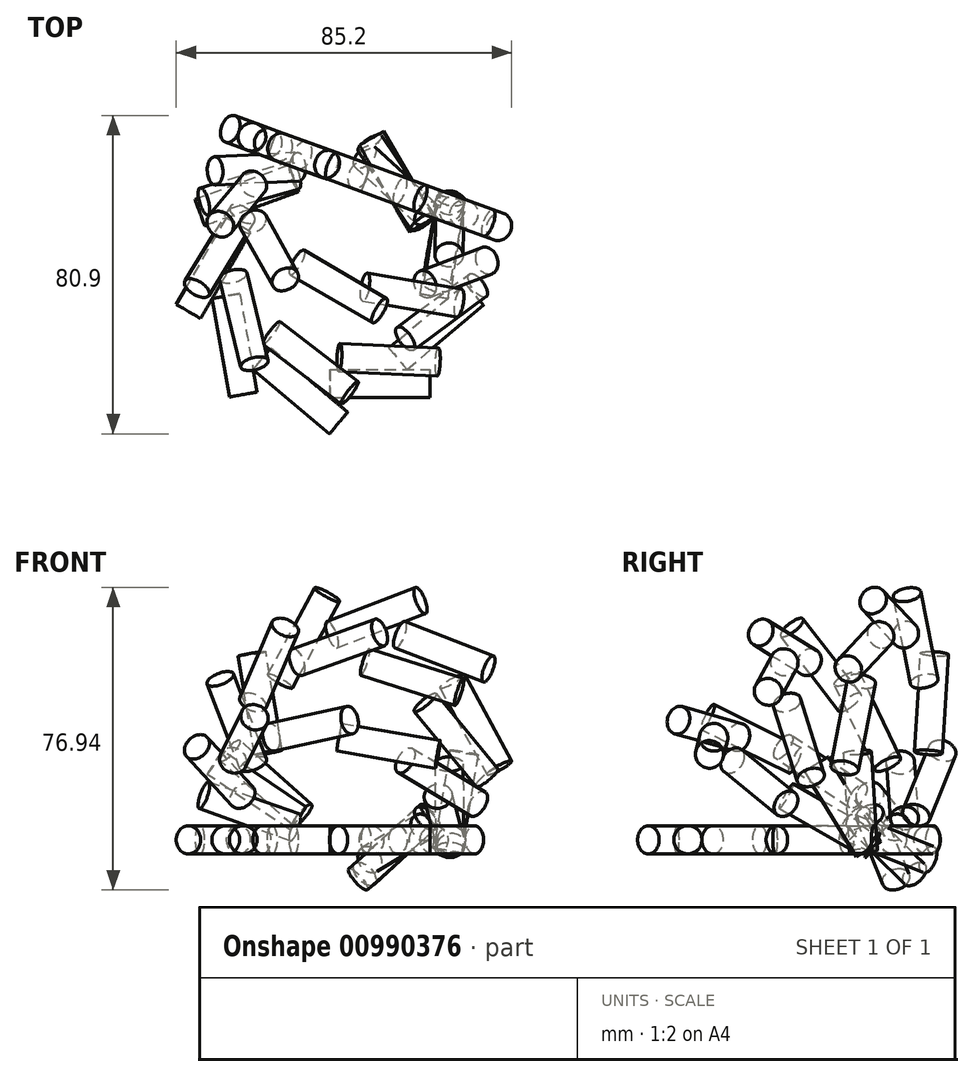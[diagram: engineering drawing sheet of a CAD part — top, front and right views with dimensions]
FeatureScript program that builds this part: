
annotation { "Feature Type Name" : "Feature", "Feature Type Description" : "" }
export const myFeature = defineFeature(function(context is Context, id is Id, definition is map)
    precondition{}
    {
        {
            var Q0;
            Q0=qCreatedBy(makeId("Right.planeOp"),FACE);
            var sketch = newSketch(context, id + "F0", { "sketchPlane" : qUnion([Q0])});
            skCircle(sketch, "E0", {"center": v(0, 0) * mm, "radius": 3.58 * mm});
            skSolve(sketch);
        }
        {
            var Q0;
            Q0=sQuery(id+"F0.wireOp",EDGE,"E0");
            extrude(context, id + "F1", {"bodyType" : ToolBodyType.SURFACE, "surfaceEntities" : qUnion([Q0]), "depth" : 25.4 * mm, "offsetDistance" : 25.4 * mm});
        }
        {
            var Q0;
            Q0=qCreatedBy(makeId("Right.planeOp"),FACE);
            var sketch = newSketch(context, id + "F2", { "sketchPlane" : qUnion([Q0])});
            skLineSegment(sketch, "E1", {"start": v(26.86, 12.55) * mm, "end": v(26.86, -32.48) * mm});
            skSolve(sketch);
        }
        {
            var Q0;
            Q0=makeQuery(id+"F1.opExtrude","SWEPT_BODY",BODY,{"disambiguationData":[OSD([sQuery(id+"F0.wireOp",EDGE,"E0")])]});
            var Q1;
            Q1=sQuery(id+"F2.wireOp",EDGE,"E1");
            circularPattern(context, id + "F3", {"entities" : qUnion([Q0]), "axis" : qUnion([Q1]), "angle" : 40 * degree, "instanceCount" : 15});
        }
        {
            var Q0;
            Q0=makeQuery(id+"F1.opExtrude","SWEPT_BODY",BODY,{"disambiguationData":[OSD([sQuery(id+"F0.wireOp",EDGE,"E0")])]});
            var Q1;
            Q1=makeQuery(id+"F3.opPattern","COPY",BODY,{"derivedFrom":makeQuery(id+"F1.opExtrude","SWEPT_BODY",BODY,{"disambiguationData":[OSD([sQuery(id+"F0.wireOp",EDGE,"E0")])]}),"instanceName":"2"});
            var Q2;
            Q2=makeQuery(id+"F3.opPattern","COPY",BODY,{"derivedFrom":makeQuery(id+"F1.opExtrude","SWEPT_BODY",BODY,{"disambiguationData":[OSD([sQuery(id+"F0.wireOp",EDGE,"E0")])]}),"instanceName":"5"});
            var Q3;
            Q3=makeQuery(id+"F3.opPattern","COPY",BODY,{"derivedFrom":makeQuery(id+"F1.opExtrude","SWEPT_BODY",BODY,{"disambiguationData":[OSD([sQuery(id+"F0.wireOp",EDGE,"E0")])]}),"instanceName":"8"});
            var Q4;
            Q4=makeQuery(id+"F3.opPattern","COPY",BODY,{"derivedFrom":makeQuery(id+"F1.opExtrude","SWEPT_BODY",BODY,{"disambiguationData":[OSD([sQuery(id+"F0.wireOp",EDGE,"E0")])]}),"instanceName":"7"});
            var Q5;
            Q5=makeQuery(id+"F3.opPattern","COPY",BODY,{"derivedFrom":makeQuery(id+"F1.opExtrude","SWEPT_BODY",BODY,{"disambiguationData":[OSD([sQuery(id+"F0.wireOp",EDGE,"E0")])]}),"instanceName":"6"});
            var Q6;
            Q6=makeQuery(id+"F3.opPattern","COPY",BODY,{"derivedFrom":makeQuery(id+"F1.opExtrude","SWEPT_BODY",BODY,{"disambiguationData":[OSD([sQuery(id+"F0.wireOp",EDGE,"E0")])]}),"instanceName":"4"});
            var Q7;
            Q7=makeQuery(id+"F3.opPattern","COPY",BODY,{"derivedFrom":makeQuery(id+"F1.opExtrude","SWEPT_BODY",BODY,{"disambiguationData":[OSD([sQuery(id+"F0.wireOp",EDGE,"E0")])]}),"instanceName":"3"});
            var Q8;
            Q8=makeQuery(id+"F3.opPattern","COPY",BODY,{"derivedFrom":makeQuery(id+"F1.opExtrude","SWEPT_BODY",BODY,{"disambiguationData":[OSD([sQuery(id+"F0.wireOp",EDGE,"E0")])]}),"instanceName":"1"});
            var Q9;
            Q9=makeQuery(id+"F3.opPattern","COPY",BODY,{"derivedFrom":makeQuery(id+"F1.opExtrude","SWEPT_BODY",BODY,{"disambiguationData":[OSD([sQuery(id+"F0.wireOp",EDGE,"E0")])]}),"instanceName":"12"});
            var Q10;
            Q10=makeQuery(id+"F3.opPattern","COPY",BODY,{"derivedFrom":makeQuery(id+"F1.opExtrude","SWEPT_BODY",BODY,{"disambiguationData":[OSD([sQuery(id+"F0.wireOp",EDGE,"E0")])]}),"instanceName":"13"});
            var Q11;
            Q11=makeQuery(id+"F3.opPattern","COPY",BODY,{"derivedFrom":makeQuery(id+"F1.opExtrude","SWEPT_BODY",BODY,{"disambiguationData":[OSD([sQuery(id+"F0.wireOp",EDGE,"E0")])]}),"instanceName":"14"});
            var Q12;
            Q12=makeQuery(id+"F3.opPattern","COPY",BODY,{"derivedFrom":makeQuery(id+"F1.opExtrude","SWEPT_BODY",BODY,{"disambiguationData":[OSD([sQuery(id+"F0.wireOp",EDGE,"E0")])]}),"instanceName":"11"});
            var Q13;
            Q13=makeQuery(id+"F3.opPattern","COPY",BODY,{"derivedFrom":makeQuery(id+"F1.opExtrude","SWEPT_BODY",BODY,{"disambiguationData":[OSD([sQuery(id+"F0.wireOp",EDGE,"E0")])]}),"instanceName":"9"});
            var Q14;
            Q14=makeQuery(id+"F3.opPattern","COPY",BODY,{"derivedFrom":makeQuery(id+"F1.opExtrude","SWEPT_BODY",BODY,{"disambiguationData":[OSD([sQuery(id+"F0.wireOp",EDGE,"E0")])]}),"instanceName":"10"});
            var Q15;
            Q15=makeQuery(id+"F3.opPattern","COPY",EDGE,{"derivedFrom":makeQuery(id+"F1.opExtrude","CAP_EDGE",EDGE,{"disambiguationData":[OSD([sQuery(id+"F0.wireOp",EDGE,"E0")])],"isStart":true}),"instanceName":"5"});
            circularPattern(context, id + "F4", {"entities" : qUnion([Q0, Q1, Q2, Q3, Q4, Q5, Q6, Q7, Q8, Q9, Q10, Q11, Q12, Q13, Q14]), "axis" : qUnion([Q15]), "angle" : 90 * degree, "instanceCount" : 4, "equalSpace" : true});
        }
    });
